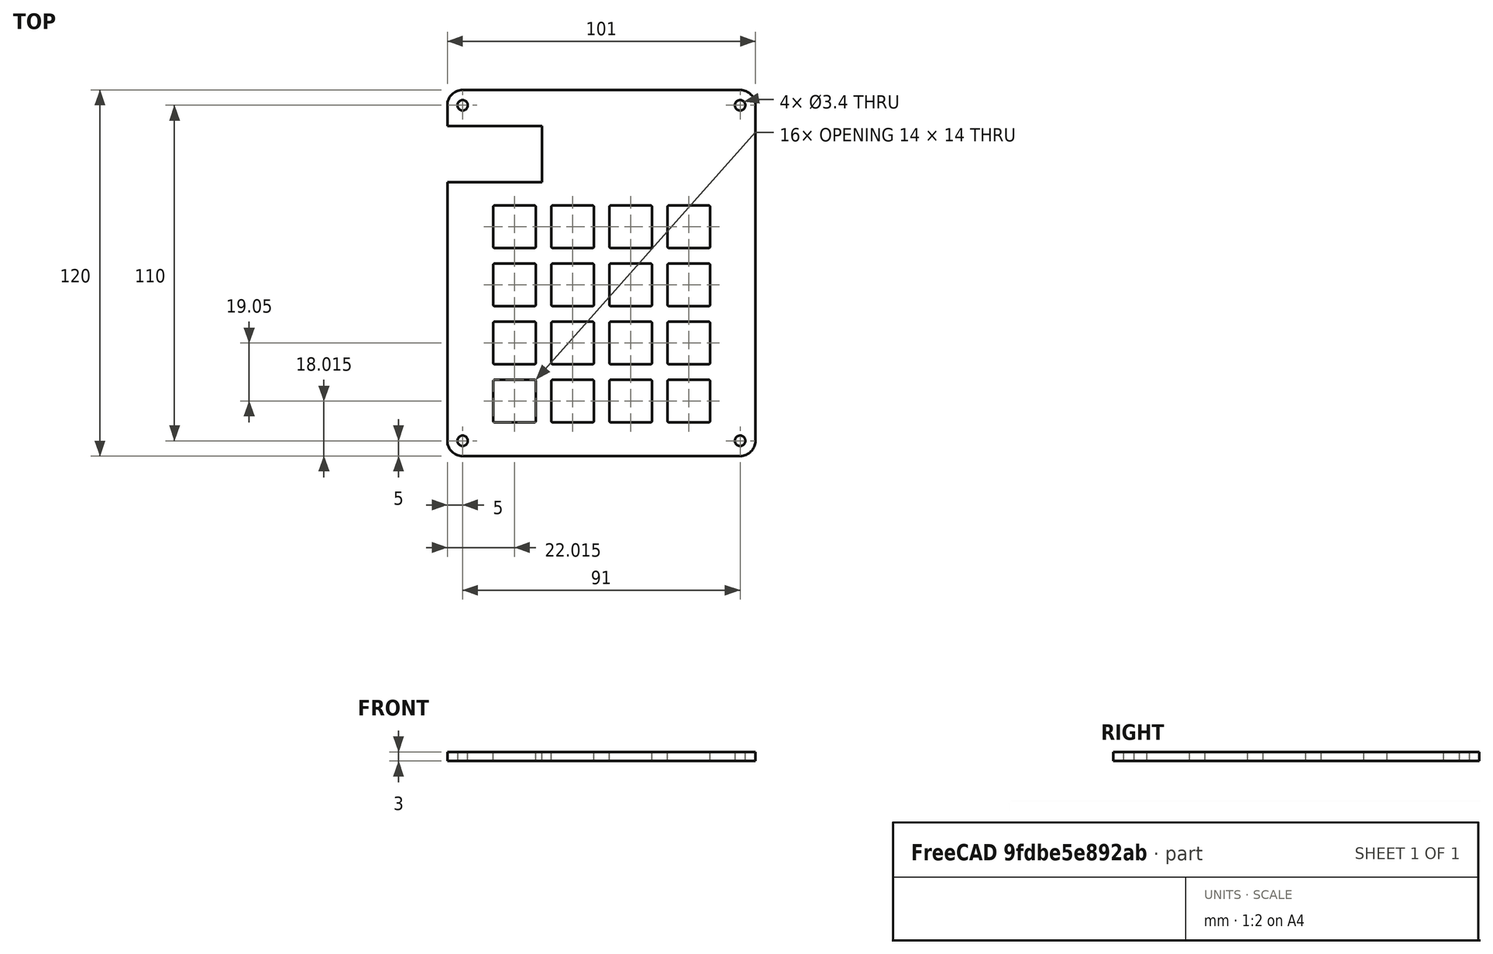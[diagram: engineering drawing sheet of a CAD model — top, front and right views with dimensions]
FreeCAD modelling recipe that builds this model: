
FCSTD DOCUMENT  (FreeCAD 1.0R39109 (Git))
Label: Plate
License: All rights reserved
LicenseURL: https://en.wikipedia.org/wiki/All_rights_reserved
objects: Sketcher::SketchObject×2, PartDesign::Pad×1, PartDesign::Pocket×1, PartDesign::Body×1
note: 11 computed .brp shape members not serialized (recipe doc carries the construction recipe); baked Part::Feature solids carry a one-line shape summary decoded from their .brp

FEATURE [Sketcher::SketchObject] Sketch  label="Keys"
  ArcFitTolerance = 1e-06
  FullyConstrained = false
  MakeInternals = false
  sketch-geometry (128):
    g0: LineSegment StartX=3.025 StartY=-2.525 StartZ=0 EndX=16.025 EndY=-2.525 EndZ=0
    g1: LineSegment StartX=3.025 StartY=-16.525 StartZ=0 EndX=16.025 EndY=-16.525 EndZ=0
    g2: LineSegment StartX=2.525 StartY=-3.025 StartZ=0 EndX=2.525 EndY=-16.025 EndZ=0
    g3: LineSegment StartX=16.525 StartY=-3.025 StartZ=0 EndX=16.525 EndY=-16.025 EndZ=0
    g4: ArcOfCircle CenterX=3.025 CenterY=-3.025 CenterZ=0 NormalX=0 NormalY=0 NormalZ=1 AngleXU=0 Radius=0.5 StartAngle=1.5708 EndAngle=3.14159
    g5: ArcOfCircle CenterX=16.025 CenterY=-3.025 CenterZ=0 NormalX=0 NormalY=0 NormalZ=1 AngleXU=0 Radius=0.5 StartAngle=0 EndAngle=1.5708
    g6: ArcOfCircle CenterX=3.025 CenterY=-16.025 CenterZ=0 NormalX=0 NormalY=0 NormalZ=1 AngleXU=0 Radius=0.5 StartAngle=3.14159 EndAngle=4.71239
    g7: ArcOfCircle CenterX=16.025 CenterY=-16.025 CenterZ=0 NormalX=0 NormalY=0 NormalZ=1 AngleXU=0 Radius=0.5 StartAngle=4.71239 EndAngle=6.28319
    g8: LineSegment StartX=22.075 StartY=-2.525 StartZ=0 EndX=35.075 EndY=-2.525 EndZ=0
    g9: LineSegment StartX=22.075 StartY=-16.525 StartZ=0 EndX=35.075 EndY=-16.525 EndZ=0
    g10: LineSegment StartX=21.575 StartY=-3.025 StartZ=0 EndX=21.575 EndY=-16.025 EndZ=0
    g11: LineSegment StartX=35.575 StartY=-3.025 StartZ=0 EndX=35.575 EndY=-16.025 EndZ=0
    g12: ArcOfCircle CenterX=22.075 CenterY=-3.025 CenterZ=0 NormalX=0 NormalY=0 NormalZ=1 AngleXU=0 Radius=0.5 StartAngle=1.5708 EndAngle=3.14159
    g13: ArcOfCircle CenterX=35.075 CenterY=-3.025 CenterZ=0 NormalX=0 NormalY=0 NormalZ=1 AngleXU=0 Radius=0.5 StartAngle=0 EndAngle=1.5708
    g14: ArcOfCircle CenterX=22.075 CenterY=-16.025 CenterZ=0 NormalX=0 NormalY=0 NormalZ=1 AngleXU=0 Radius=0.5 StartAngle=3.14159 EndAngle=4.71239
    g15: ArcOfCircle CenterX=35.075 CenterY=-16.025 CenterZ=0 NormalX=0 NormalY=0 NormalZ=1 AngleXU=0 Radius=0.5 StartAngle=4.71239 EndAngle=6.28319
    g16: LineSegment StartX=41.125 StartY=-2.525 StartZ=0 EndX=54.125 EndY=-2.525 EndZ=0
    g17: LineSegment StartX=41.125 StartY=-16.525 StartZ=0 EndX=54.125 EndY=-16.525 EndZ=0
    g18: LineSegment StartX=40.625 StartY=-3.025 StartZ=0 EndX=40.625 EndY=-16.025 EndZ=0
    g19: LineSegment StartX=54.625 StartY=-3.025 StartZ=0 EndX=54.625 EndY=-16.025 EndZ=0
    g20: ArcOfCircle CenterX=41.125 CenterY=-3.025 CenterZ=0 NormalX=0 NormalY=0 NormalZ=1 AngleXU=0 Radius=0.5 StartAngle=1.5708 EndAngle=3.14159
    g21: ArcOfCircle CenterX=54.125 CenterY=-3.025 CenterZ=0 NormalX=0 NormalY=0 NormalZ=1 AngleXU=0 Radius=0.5 StartAngle=0 EndAngle=1.5708
    g22: ArcOfCircle CenterX=41.125 CenterY=-16.025 CenterZ=0 NormalX=0 NormalY=0 NormalZ=1 AngleXU=0 Radius=0.5 StartAngle=3.14159 EndAngle=4.71239
    g23: ArcOfCircle CenterX=54.125 CenterY=-16.025 CenterZ=0 NormalX=0 NormalY=0 NormalZ=1 AngleXU=0 Radius=0.5 StartAngle=4.71239 EndAngle=6.28319
    g24: LineSegment StartX=60.175 StartY=-2.525 StartZ=0 EndX=73.175 EndY=-2.525 EndZ=0
    g25: LineSegment StartX=60.175 StartY=-16.525 StartZ=0 EndX=73.175 EndY=-16.525 EndZ=0
    g26: LineSegment StartX=59.675 StartY=-3.025 StartZ=0 EndX=59.675 EndY=-16.025 EndZ=0
    g27: LineSegment StartX=73.675 StartY=-3.025 StartZ=0 EndX=73.675 EndY=-16.025 EndZ=0
    g28: ArcOfCircle CenterX=60.175 CenterY=-3.025 CenterZ=0 NormalX=0 NormalY=0 NormalZ=1 AngleXU=0 Radius=0.5 StartAngle=1.5708 EndAngle=3.14159
    g29: ArcOfCircle CenterX=73.175 CenterY=-3.025 CenterZ=0 NormalX=0 NormalY=0 NormalZ=1 AngleXU=0 Radius=0.5 StartAngle=0 EndAngle=1.5708
    g30: ArcOfCircle CenterX=60.175 CenterY=-16.025 CenterZ=0 NormalX=0 NormalY=0 NormalZ=1 AngleXU=0 Radius=0.5 StartAngle=3.14159 EndAngle=4.71239
    g31: ArcOfCircle CenterX=73.175 CenterY=-16.025 CenterZ=0 NormalX=0 NormalY=0 NormalZ=1 AngleXU=0 Radius=0.5 StartAngle=4.71239 EndAngle=6.28319
    g32: LineSegment StartX=3.025 StartY=-21.575 StartZ=0 EndX=16.025 EndY=-21.575 EndZ=0
    g33: LineSegment StartX=3.025 StartY=-35.575 StartZ=0 EndX=16.025 EndY=-35.575 EndZ=0
    g34: LineSegment StartX=2.525 StartY=-22.075 StartZ=0 EndX=2.525 EndY=-35.075 EndZ=0
    g35: LineSegment StartX=16.525 StartY=-22.075 StartZ=0 EndX=16.525 EndY=-35.075 EndZ=0
    g36: ArcOfCircle CenterX=3.025 CenterY=-22.075 CenterZ=0 NormalX=0 NormalY=0 NormalZ=1 AngleXU=0 Radius=0.5 StartAngle=1.5708 EndAngle=3.14159
    g37: ArcOfCircle CenterX=16.025 CenterY=-22.075 CenterZ=0 NormalX=0 NormalY=0 NormalZ=1 AngleXU=0 Radius=0.5 StartAngle=0 EndAngle=1.5708
    g38: ArcOfCircle CenterX=3.025 CenterY=-35.075 CenterZ=0 NormalX=0 NormalY=0 NormalZ=1 AngleXU=0 Radius=0.5 StartAngle=3.14159 EndAngle=4.71239
    g39: ArcOfCircle CenterX=16.025 CenterY=-35.075 CenterZ=0 NormalX=0 NormalY=0 NormalZ=1 AngleXU=0 Radius=0.5 StartAngle=4.71239 EndAngle=6.28319
    g40: LineSegment StartX=22.075 StartY=-21.575 StartZ=0 EndX=35.075 EndY=-21.575 EndZ=0
    g41: LineSegment StartX=22.075 StartY=-35.575 StartZ=0 EndX=35.075 EndY=-35.575 EndZ=0
    g42: LineSegment StartX=21.575 StartY=-22.075 StartZ=0 EndX=21.575 EndY=-35.075 EndZ=0
    g43: LineSegment StartX=35.575 StartY=-22.075 StartZ=0 EndX=35.575 EndY=-35.075 EndZ=0
    g44: ArcOfCircle CenterX=22.075 CenterY=-22.075 CenterZ=0 NormalX=0 NormalY=0 NormalZ=1 AngleXU=0 Radius=0.5 StartAngle=1.5708 EndAngle=3.14159
    g45: ArcOfCircle CenterX=35.075 CenterY=-22.075 CenterZ=0 NormalX=0 NormalY=0 NormalZ=1 AngleXU=0 Radius=0.5 StartAngle=0 EndAngle=1.5708
    g46: ArcOfCircle CenterX=22.075 CenterY=-35.075 CenterZ=0 NormalX=0 NormalY=0 NormalZ=1 AngleXU=0 Radius=0.5 StartAngle=3.14159 EndAngle=4.71239
    g47: ArcOfCircle CenterX=35.075 CenterY=-35.075 CenterZ=0 NormalX=0 NormalY=0 NormalZ=1 AngleXU=0 Radius=0.5 StartAngle=4.71239 EndAngle=6.28319
    g48: LineSegment StartX=41.125 StartY=-21.575 StartZ=0 EndX=54.125 EndY=-21.575 EndZ=0
    g49: LineSegment StartX=41.125 StartY=-35.575 StartZ=0 EndX=54.125 EndY=-35.575 EndZ=0
    g50: LineSegment StartX=40.625 StartY=-22.075 StartZ=0 EndX=40.625 EndY=-35.075 EndZ=0
    g51: LineSegment StartX=54.625 StartY=-22.075 StartZ=0 EndX=54.625 EndY=-35.075 EndZ=0
    g52: ArcOfCircle CenterX=41.125 CenterY=-22.075 CenterZ=0 NormalX=0 NormalY=0 NormalZ=1 AngleXU=0 Radius=0.5 StartAngle=1.5708 EndAngle=3.14159
    g53: ArcOfCircle CenterX=54.125 CenterY=-22.075 CenterZ=0 NormalX=0 NormalY=0 NormalZ=1 AngleXU=0 Radius=0.5 StartAngle=0 EndAngle=1.5708
    g54: ArcOfCircle CenterX=41.125 CenterY=-35.075 CenterZ=0 NormalX=0 NormalY=0 NormalZ=1 AngleXU=0 Radius=0.5 StartAngle=3.14159 EndAngle=4.71239
    g55: ArcOfCircle CenterX=54.125 CenterY=-35.075 CenterZ=0 NormalX=0 NormalY=0 NormalZ=1 AngleXU=0 Radius=0.5 StartAngle=4.71239 EndAngle=6.28319
    g56: LineSegment StartX=60.175 StartY=-21.575 StartZ=0 EndX=73.175 EndY=-21.575 EndZ=0
    g57: LineSegment StartX=60.175 StartY=-35.575 StartZ=0 EndX=73.175 EndY=-35.575 EndZ=0
    g58: LineSegment StartX=59.675 StartY=-22.075 StartZ=0 EndX=59.675 EndY=-35.075 EndZ=0
    g59: LineSegment StartX=73.675 StartY=-22.075 StartZ=0 EndX=73.675 EndY=-35.075 EndZ=0
    g60: ArcOfCircle CenterX=60.175 CenterY=-22.075 CenterZ=0 NormalX=0 NormalY=0 NormalZ=1 AngleXU=0 Radius=0.5 StartAngle=1.5708 EndAngle=3.14159
    g61: ArcOfCircle CenterX=73.175 CenterY=-22.075 CenterZ=0 NormalX=0 NormalY=0 NormalZ=1 AngleXU=0 Radius=0.5 StartAngle=0 EndAngle=1.5708
    g62: ArcOfCircle CenterX=60.175 CenterY=-35.075 CenterZ=0 NormalX=0 NormalY=0 NormalZ=1 AngleXU=0 Radius=0.5 StartAngle=3.14159 EndAngle=4.71239
    g63: ArcOfCircle CenterX=73.175 CenterY=-35.075 CenterZ=0 NormalX=0 NormalY=0 NormalZ=1 AngleXU=0 Radius=0.5 StartAngle=4.71239 EndAngle=6.28319
    g64: LineSegment StartX=3.025 StartY=-40.625 StartZ=0 EndX=16.025 EndY=-40.625 EndZ=0
    g65: LineSegment StartX=3.025 StartY=-54.625 StartZ=0 EndX=16.025 EndY=-54.625 EndZ=0
    g66: LineSegment StartX=2.525 StartY=-41.125 StartZ=0 EndX=2.525 EndY=-54.125 EndZ=0
    g67: LineSegment StartX=16.525 StartY=-41.125 StartZ=0 EndX=16.525 EndY=-54.125 EndZ=0
    g68: ArcOfCircle CenterX=3.025 CenterY=-41.125 CenterZ=0 NormalX=0 NormalY=0 NormalZ=1 AngleXU=0 Radius=0.5 StartAngle=1.5708 EndAngle=3.14159
    g69: ArcOfCircle CenterX=16.025 CenterY=-41.125 CenterZ=0 NormalX=0 NormalY=0 NormalZ=1 AngleXU=0 Radius=0.5 StartAngle=0 EndAngle=1.5708
    g70: ArcOfCircle CenterX=3.025 CenterY=-54.125 CenterZ=0 NormalX=0 NormalY=0 NormalZ=1 AngleXU=0 Radius=0.5 StartAngle=3.14159 EndAngle=4.71239
    g71: ArcOfCircle CenterX=16.025 CenterY=-54.125 CenterZ=0 NormalX=0 NormalY=0 NormalZ=1 AngleXU=0 Radius=0.5 StartAngle=4.71239 EndAngle=6.28319
    g72: LineSegment StartX=22.075 StartY=-40.625 StartZ=0 EndX=35.075 EndY=-40.625 EndZ=0
    g73: LineSegment StartX=22.075 StartY=-54.625 StartZ=0 EndX=35.075 EndY=-54.625 EndZ=0
    g74: LineSegment StartX=21.575 StartY=-41.125 StartZ=0 EndX=21.575 EndY=-54.125 EndZ=0
    g75: LineSegment StartX=35.575 StartY=-41.125 StartZ=0 EndX=35.575 EndY=-54.125 EndZ=0
    g76: ArcOfCircle CenterX=22.075 CenterY=-41.125 CenterZ=0 NormalX=0 NormalY=0 NormalZ=1 AngleXU=0 Radius=0.5 StartAngle=1.5708 EndAngle=3.14159
    g77: ArcOfCircle CenterX=35.075 CenterY=-41.125 CenterZ=0 NormalX=0 NormalY=0 NormalZ=1 AngleXU=0 Radius=0.5 StartAngle=0 EndAngle=1.5708
    g78: ArcOfCircle CenterX=22.075 CenterY=-54.125 CenterZ=0 NormalX=0 NormalY=0 NormalZ=1 AngleXU=0 Radius=0.5 StartAngle=3.14159 EndAngle=4.71239
    g79: ArcOfCircle CenterX=35.075 CenterY=-54.125 CenterZ=0 NormalX=0 NormalY=0 NormalZ=1 AngleXU=0 Radius=0.5 StartAngle=4.71239 EndAngle=6.28319
    g80: LineSegment StartX=41.125 StartY=-40.625 StartZ=0 EndX=54.125 EndY=-40.625 EndZ=0
    g81: LineSegment StartX=41.125 StartY=-54.625 StartZ=0 EndX=54.125 EndY=-54.625 EndZ=0
    g82: LineSegment StartX=40.625 StartY=-41.125 StartZ=0 EndX=40.625 EndY=-54.125 EndZ=0
    g83: LineSegment StartX=54.625 StartY=-41.125 StartZ=0 EndX=54.625 EndY=-54.125 EndZ=0
    g84: ArcOfCircle CenterX=41.125 CenterY=-41.125 CenterZ=0 NormalX=0 NormalY=0 NormalZ=1 AngleXU=0 Radius=0.5 StartAngle=1.5708 EndAngle=3.14159
    g85: ArcOfCircle CenterX=54.125 CenterY=-41.125 CenterZ=0 NormalX=0 NormalY=0 NormalZ=1 AngleXU=0 Radius=0.5 StartAngle=0 EndAngle=1.5708
    g86: ArcOfCircle CenterX=41.125 CenterY=-54.125 CenterZ=0 NormalX=0 NormalY=0 NormalZ=1 AngleXU=0 Radius=0.5 StartAngle=3.14159 EndAngle=4.71239
    g87: ArcOfCircle CenterX=54.125 CenterY=-54.125 CenterZ=0 NormalX=0 NormalY=0 NormalZ=1 AngleXU=0 Radius=0.5 StartAngle=4.71239 EndAngle=6.28319
    g88: LineSegment StartX=60.175 StartY=-40.625 StartZ=0 EndX=73.175 EndY=-40.625 EndZ=0
    g89: LineSegment StartX=60.175 StartY=-54.625 StartZ=0 EndX=73.175 EndY=-54.625 EndZ=0
    g90: LineSegment StartX=59.675 StartY=-41.125 StartZ=0 EndX=59.675 EndY=-54.125 EndZ=0
    g91: LineSegment StartX=73.675 StartY=-41.125 StartZ=0 EndX=73.675 EndY=-54.125 EndZ=0
    g92: ArcOfCircle CenterX=60.175 CenterY=-41.125 CenterZ=0 NormalX=0 NormalY=0 NormalZ=1 AngleXU=0 Radius=0.5 StartAngle=1.5708 EndAngle=3.14159
    g93: ArcOfCircle CenterX=73.175 CenterY=-41.125 CenterZ=0 NormalX=0 NormalY=0 NormalZ=1 AngleXU=0 Radius=0.5 StartAngle=0 EndAngle=1.5708
    g94: ArcOfCircle CenterX=60.175 CenterY=-54.125 CenterZ=0 NormalX=0 NormalY=0 NormalZ=1 AngleXU=0 Radius=0.5 StartAngle=3.14159 EndAngle=4.71239
    g95: ArcOfCircle CenterX=73.175 CenterY=-54.125 CenterZ=0 NormalX=0 NormalY=0 NormalZ=1 AngleXU=0 Radius=0.5 StartAngle=4.71239 EndAngle=6.28319
    g96: LineSegment StartX=3.025 StartY=-59.675 StartZ=0 EndX=16.025 EndY=-59.675 EndZ=0
    g97: LineSegment StartX=3.025 StartY=-73.675 StartZ=0 EndX=16.025 EndY=-73.675 EndZ=0
    g98: LineSegment StartX=2.525 StartY=-60.175 StartZ=0 EndX=2.525 EndY=-73.175 EndZ=0
    g99: LineSegment StartX=16.525 StartY=-60.175 StartZ=0 EndX=16.525 EndY=-73.175 EndZ=0
    g100: ArcOfCircle CenterX=3.025 CenterY=-60.175 CenterZ=0 NormalX=0 NormalY=0 NormalZ=1 AngleXU=0 Radius=0.5 StartAngle=1.5708 EndAngle=3.14159
    g101: ArcOfCircle CenterX=16.025 CenterY=-60.175 CenterZ=0 NormalX=0 NormalY=0 NormalZ=1 AngleXU=0 Radius=0.5 StartAngle=0 EndAngle=1.5708
    g102: ArcOfCircle CenterX=3.025 CenterY=-73.175 CenterZ=0 NormalX=0 NormalY=0 NormalZ=1 AngleXU=0 Radius=0.5 StartAngle=3.14159 EndAngle=4.71239
    g103: ArcOfCircle CenterX=16.025 CenterY=-73.175 CenterZ=0 NormalX=0 NormalY=0 NormalZ=1 AngleXU=0 Radius=0.5 StartAngle=4.71239 EndAngle=6.28319
    g104: LineSegment StartX=22.075 StartY=-59.675 StartZ=0 EndX=35.075 EndY=-59.675 EndZ=0
    g105: LineSegment StartX=22.075 StartY=-73.675 StartZ=0 EndX=35.075 EndY=-73.675 EndZ=0
    g106: LineSegment StartX=21.575 StartY=-60.175 StartZ=0 EndX=21.575 EndY=-73.175 EndZ=0
    g107: LineSegment StartX=35.575 StartY=-60.175 StartZ=0 EndX=35.575 EndY=-73.175 EndZ=0
    g108: ArcOfCircle CenterX=22.075 CenterY=-60.175 CenterZ=0 NormalX=0 NormalY=0 NormalZ=1 AngleXU=0 Radius=0.5 StartAngle=1.5708 EndAngle=3.14159
    g109: ArcOfCircle CenterX=35.075 CenterY=-60.175 CenterZ=0 NormalX=0 NormalY=0 NormalZ=1 AngleXU=0 Radius=0.5 StartAngle=0 EndAngle=1.5708
    g110: ArcOfCircle CenterX=22.075 CenterY=-73.175 CenterZ=0 NormalX=0 NormalY=0 NormalZ=1 AngleXU=0 Radius=0.5 StartAngle=3.14159 EndAngle=4.71239
    g111: ArcOfCircle CenterX=35.075 CenterY=-73.175 CenterZ=0 NormalX=0 NormalY=0 NormalZ=1 AngleXU=0 Radius=0.5 StartAngle=4.71239 EndAngle=6.28319
    g112: LineSegment StartX=41.125 StartY=-59.675 StartZ=0 EndX=54.125 EndY=-59.675 EndZ=0
    g113: LineSegment StartX=41.125 StartY=-73.675 StartZ=0 EndX=54.125 EndY=-73.675 EndZ=0
    g114: LineSegment StartX=40.625 StartY=-60.175 StartZ=0 EndX=40.625 EndY=-73.175 EndZ=0
    g115: LineSegment StartX=54.625 StartY=-60.175 StartZ=0 EndX=54.625 EndY=-73.175 EndZ=0
    g116: ArcOfCircle CenterX=41.125 CenterY=-60.175 CenterZ=0 NormalX=0 NormalY=0 NormalZ=1 AngleXU=0 Radius=0.5 StartAngle=1.5708 EndAngle=3.14159
    g117: ArcOfCircle CenterX=54.125 CenterY=-60.175 CenterZ=0 NormalX=0 NormalY=0 NormalZ=1 AngleXU=0 Radius=0.5 StartAngle=0 EndAngle=1.5708
    g118: ArcOfCircle CenterX=41.125 CenterY=-73.175 CenterZ=0 NormalX=0 NormalY=0 NormalZ=1 AngleXU=0 Radius=0.5 StartAngle=3.14159 EndAngle=4.71239
    g119: ArcOfCircle CenterX=54.125 CenterY=-73.175 CenterZ=0 NormalX=0 NormalY=0 NormalZ=1 AngleXU=0 Radius=0.5 StartAngle=4.71239 EndAngle=6.28319
    g120: LineSegment StartX=60.175 StartY=-59.675 StartZ=0 EndX=73.175 EndY=-59.675 EndZ=0
    g121: LineSegment StartX=60.175 StartY=-73.675 StartZ=0 EndX=73.175 EndY=-73.675 EndZ=0
    g122: LineSegment StartX=59.675 StartY=-60.175 StartZ=0 EndX=59.675 EndY=-73.175 EndZ=0
    g123: LineSegment StartX=73.675 StartY=-60.175 StartZ=0 EndX=73.675 EndY=-73.175 EndZ=0
    g124: ArcOfCircle CenterX=60.175 CenterY=-60.175 CenterZ=0 NormalX=0 NormalY=0 NormalZ=1 AngleXU=0 Radius=0.5 StartAngle=1.5708 EndAngle=3.14159
    g125: ArcOfCircle CenterX=73.175 CenterY=-60.175 CenterZ=0 NormalX=0 NormalY=0 NormalZ=1 AngleXU=0 Radius=0.5 StartAngle=0 EndAngle=1.5708
    g126: ArcOfCircle CenterX=60.175 CenterY=-73.175 CenterZ=0 NormalX=0 NormalY=0 NormalZ=1 AngleXU=0 Radius=0.5 StartAngle=3.14159 EndAngle=4.71239
    g127: ArcOfCircle CenterX=73.175 CenterY=-73.175 CenterZ=0 NormalX=0 NormalY=0 NormalZ=1 AngleXU=0 Radius=0.5 StartAngle=4.71239 EndAngle=6.28319
  constraints (128):
    c: Coincident(g98,g102)
    c: Coincident(g98,g100)
    c: Coincident(g66,g70)
    c: Coincident(g66,g68)
    c: Coincident(g34,g38)
    c: Coincident(g34,g36)
    c: Coincident(g2,g6)
    c: Coincident(g2,g4)
    c: Coincident(g97,g102)
    c: Coincident(g96,g100)
    c: Coincident(g65,g70)
    c: Coincident(g64,g68)
    c: Coincident(g33,g38)
    c: Coincident(g32,g36)
    c: Coincident(g1,g6)
    c: Coincident(g0,g4)
    c: Coincident(g97,g103)
    c: Coincident(g96,g101)
    c: Coincident(g65,g71)
    c: Coincident(g64,g69)
    c: Coincident(g33,g39)
    c: Coincident(g32,g37)
    c: Coincident(g1,g7)
    c: Coincident(g0,g5)
    c: Coincident(g99,g103)
    c: Coincident(g99,g101)
    c: Coincident(g67,g71)
    c: Coincident(g67,g69)
    c: Coincident(g35,g39)
    c: Coincident(g35,g37)
    c: Coincident(g3,g7)
    c: Coincident(g3,g5)
    c: Coincident(g106,g110)
    c: Coincident(g106,g108)
    c: Coincident(g74,g78)
    c: Coincident(g74,g76)
    c: Coincident(g42,g46)
    c: Coincident(g42,g44)
    c: Coincident(g10,g14)
    c: Coincident(g10,g12)
    c: Coincident(g105,g110)
    c: Coincident(g104,g108)
    c: Coincident(g73,g78)
    c: Coincident(g72,g76)
    c: Coincident(g41,g46)
    c: Coincident(g40,g44)
    c: Coincident(g9,g14)
    c: Coincident(g8,g12)
    c: Coincident(g105,g111)
    c: Coincident(g104,g109)
    c: Coincident(g73,g79)
    c: Coincident(g72,g77)
    c: Coincident(g41,g47)
    c: Coincident(g40,g45)
    c: Coincident(g9,g15)
    c: Coincident(g8,g13)
    c: Coincident(g107,g111)
    c: Coincident(g107,g109)
    c: Coincident(g75,g79)
    c: Coincident(g75,g77)
    c: Coincident(g43,g47)
    c: Coincident(g43,g45)
    c: Coincident(g11,g15)
    c: Coincident(g11,g13)
    c: Coincident(g114,g118)
    c: Coincident(g114,g116)
    c: Coincident(g82,g86)
    c: Coincident(g82,g84)
    c: Coincident(g50,g54)
    c: Coincident(g50,g52)
    c: Coincident(g18,g22)
    c: Coincident(g18,g20)
    c: Coincident(g113,g118)
    c: Coincident(g112,g116)
    c: Coincident(g81,g86)
    c: Coincident(g80,g84)
    c: Coincident(g49,g54)
    c: Coincident(g48,g52)
    c: Coincident(g17,g22)
    c: Coincident(g16,g20)
    c: Coincident(g113,g119)
    c: Coincident(g112,g117)
    c: Coincident(g81,g87)
    c: Coincident(g80,g85)
    c: Coincident(g49,g55)
    c: Coincident(g48,g53)
    c: Coincident(g17,g23)
    c: Coincident(g16,g21)
    c: Coincident(g115,g119)
    c: Coincident(g115,g117)
    c: Coincident(g83,g87)
    c: Coincident(g83,g85)
    c: Coincident(g51,g55)
    c: Coincident(g51,g53)
    c: Coincident(g19,g23)
    c: Coincident(g19,g21)
    c: Coincident(g122,g126)
    c: Coincident(g122,g124)
    c: Coincident(g90,g94)
    c: Coincident(g90,g92)
    c: Coincident(g58,g62)
    c: Coincident(g58,g60)
    c: Coincident(g26,g30)
    c: Coincident(g26,g28)
    c: Coincident(g121,g126)
    c: Coincident(g120,g124)
    c: Coincident(g89,g94)
    c: Coincident(g88,g92)
    c: Coincident(g57,g62)
    c: Coincident(g56,g60)
    c: Coincident(g25,g30)
    c: Coincident(g24,g28)
    c: Coincident(g121,g127)
    c: Coincident(g120,g125)
    c: Coincident(g89,g95)
    c: Coincident(g88,g93)
    c: Coincident(g57,g63)
    c: Coincident(g56,g61)
    c: Coincident(g25,g31)
    c: Coincident(g24,g29)
    c: Coincident(g123,g127)
    c: Coincident(g123,g125)
    c: Coincident(g91,g95)
    c: Coincident(g91,g93)
    c: Coincident(g59,g63)
    c: Coincident(g59,g61)
    c: Coincident(g27,g31)
    c: Coincident(g27,g29)
FEATURE [Sketcher::SketchObject] Sketch001  label="Plate"
  ArcFitTolerance = 1e-06
  AttachmentSupport = -> [XY_Plane]
  ExternalGeometry = -> [Sketch]
  FullyConstrained = false
  MakeInternals = false
  MapMode = 5
  sketch-geometry (18):
    g0: LineSegment StartX=-12.49 StartY=30.31 StartZ=0 EndX=-12.49 EndY=23.56 EndZ=0
    g1: LineSegment StartX=-7.49 StartY=-84.69 StartZ=0 EndX=83.51 EndY=-84.69 EndZ=0
    g2: LineSegment StartX=88.51 StartY=-79.69 StartZ=0 EndX=88.51 EndY=30.31 EndZ=0
    g3: LineSegment StartX=83.51 StartY=35.31 StartZ=0 EndX=-7.49 EndY=35.31 EndZ=0
    g4: ArcOfCircle CenterX=-7.49 CenterY=30.31 CenterZ=0 NormalX=0 NormalY=0 NormalZ=1 AngleXU=0 Radius=5 StartAngle=1.5708 EndAngle=3.14159
    g5: ArcOfCircle CenterX=-7.49 CenterY=-79.69 CenterZ=0 NormalX=0 NormalY=0 NormalZ=1 AngleXU=0 Radius=5 StartAngle=3.14159 EndAngle=4.71239
    g6: ArcOfCircle CenterX=83.51 CenterY=-79.69 CenterZ=0 NormalX=0 NormalY=0 NormalZ=1 AngleXU=0 Radius=5 StartAngle=4.71239 EndAngle=6.28319
    g7: ArcOfCircle CenterX=83.51 CenterY=30.31 CenterZ=0 NormalX=0 NormalY=0 NormalZ=1 AngleXU=0 Radius=5 StartAngle=0 EndAngle=1.5708
    g8: GeomPoint [constr] X=-12.49 Y=35.31 Z=0
    g9: GeomPoint [constr] X=88.51 Y=-84.69 Z=0
    g10: Circle CenterX=-7.49 CenterY=-79.69 CenterZ=0 NormalX=0 NormalY=0 NormalZ=1 AngleXU=0 Radius=1.7
    g11: Circle CenterX=83.51 CenterY=-79.69 CenterZ=0 NormalX=0 NormalY=0 NormalZ=1 AngleXU=0 Radius=1.7
    g12: Circle CenterX=83.51 CenterY=30.31 CenterZ=0 NormalX=0 NormalY=0 NormalZ=1 AngleXU=0 Radius=1.7
    g13: Circle CenterX=-7.49 CenterY=30.31 CenterZ=0 NormalX=0 NormalY=0 NormalZ=1 AngleXU=0 Radius=1.7
    g14: LineSegment StartX=-12.49 StartY=5.06 StartZ=0 EndX=18.51 EndY=5.06 EndZ=0
    g15: LineSegment StartX=18.51 StartY=5.06 StartZ=0 EndX=18.51 EndY=23.56 EndZ=0
    g16: LineSegment StartX=18.51 StartY=23.56 StartZ=0 EndX=-12.49 EndY=23.56 EndZ=0
    g17: LineSegment StartX=-12.49 StartY=5.06 StartZ=0 EndX=-12.49 EndY=-79.69 EndZ=0
  constraints (44):
    c: Tangent(g0,g4) = -1.5708
    c: Coincident(g17,g5) = -1.5708
    c: Tangent(g1,g5) = -1.5708
    c: Tangent(g1,g6) = -1.5708
    c: Tangent(g2,g6) = -1.5708
    c: Tangent(g2,g7) = -1.5708
    c: Tangent(g3,g7) = -1.5708
    c: Tangent(g3,g4) = -1.5708
    c: Vertical(g0)
    c: Vertical(g2)
    c: Horizontal(g1)
    c: Horizontal(g3)
    c: Equal(g4,g5)
    c: Equal(g5,g6)
    c: Equal(g6,g7)
    c: PointOnObject(g8,g0)
    c: PointOnObject(g8,g3)
    c: PointOnObject(g9,g1)
    c: PointOnObject(g9,g2)
    c: Radius(g4) = 5
    c: DistanceX(g3,g3) = 91
    c: DistanceY(g2,g2) = 110
    c: Distance(g0,g-3) = 15.015
    c: Distance(g1,g-4) = 11.015
    c: Diameter(g10) = 3.4
    c: Diameter(g11) = 3.4
    c: Diameter(g12) = 3.4
    c: Distance(g12,g3) = 5
    c: Distance(g12,g2) = 5
    c: Diameter(g13) = 3.4
    c: Distance(g13,g3) = 5
    c: Distance(g13,g0) = 5
    c: Distance(g10,g1) = 5
    c: Distance(g10,g0) = 5
    c: Distance(g11,g2) = 5
    c: Distance(g11,g1) = 5
    c: Coincident(g14,g15)
    c: Coincident(g15,g16)
    c: Vertical(g15)
    c: Horizontal(g14)
    c: Horizontal(g16)
    c: DistanceX(g16,g16) = 31
    c: DistanceY(g14,g16) = 18.5
    c: Distance(g16,g3) = 11.75
FEATURE [PartDesign::Pad] Pad
  Direction = (0,0,1)
  Length = 3
  Length2 = 10
  Profile = -> Sketch001
  ReferenceAxis = -> Sketch001 [N_Axis]
  Refine = true
  Suppressed = false
  Type = 0
FEATURE [PartDesign::Pocket] Pocket
  BaseFeature = -> Pad
  Direction = (0,0,-1)
  Length = 10
  Length2 = 5
  Profile = -> Sketch
  ReferenceAxis = -> Sketch [N_Axis]
  Refine = true
  Reversed = true
  Suppressed = false
  Type = 0
FEATURE [PartDesign::Body] Body
  AllowCompound = false
  Group = -> [Sketch001,Sketch,Pad,Pocket]
  Origin = -> Origin
  Tip = -> Pocket
